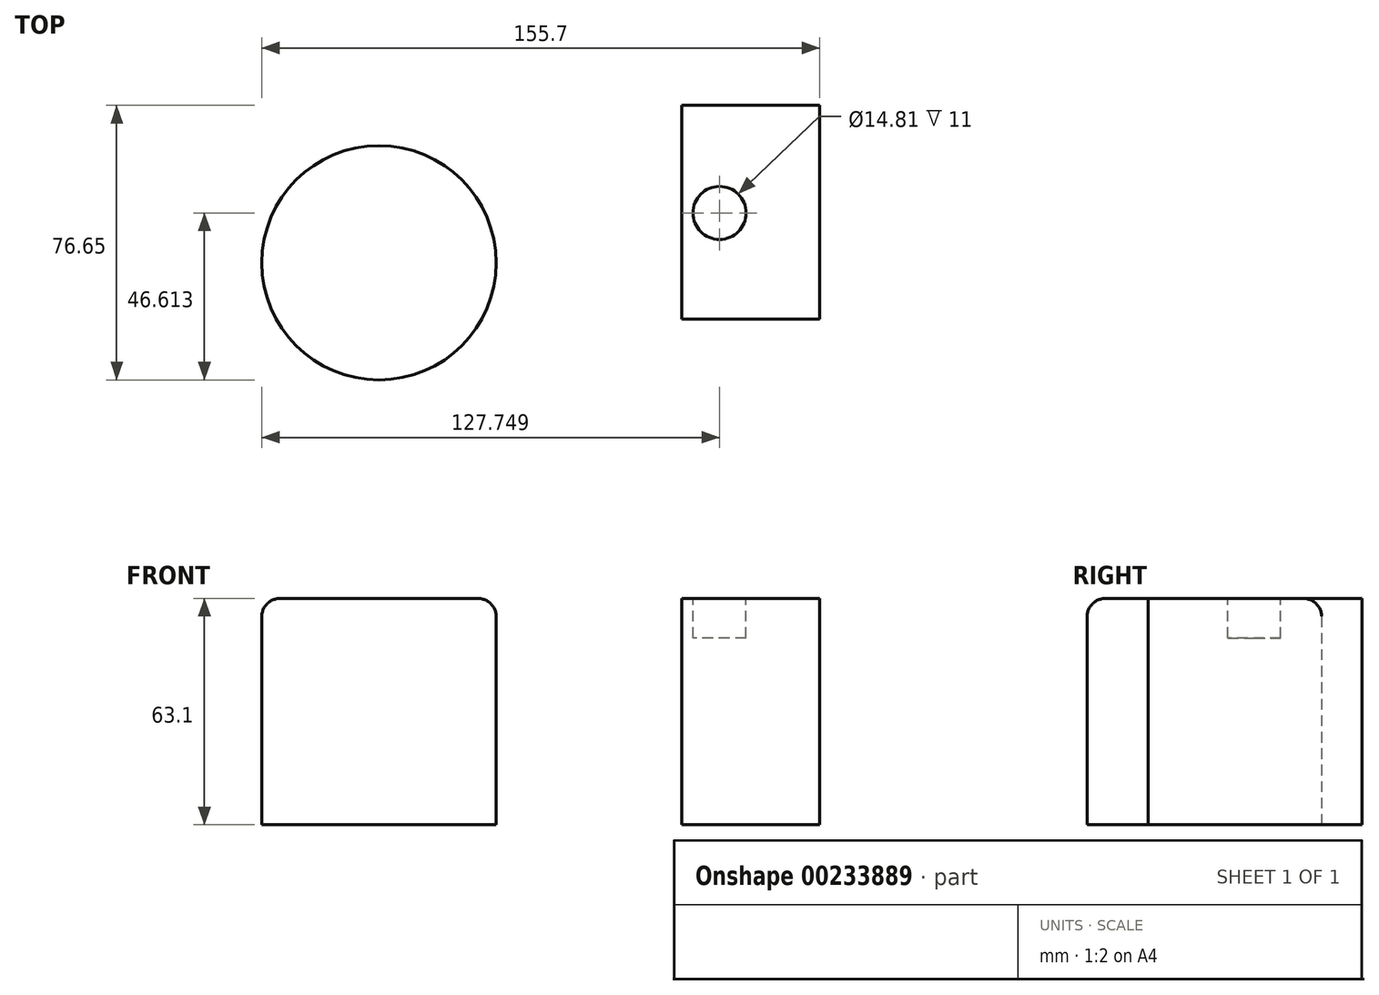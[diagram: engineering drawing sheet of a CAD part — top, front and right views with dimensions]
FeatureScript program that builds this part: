
annotation { "Feature Type Name" : "Feature", "Feature Type Description" : "" }
export const myFeature = defineFeature(function(context is Context, id is Id, definition is map)
    precondition{}
    {
        {
            var Q0;
            Q0=qCreatedBy(makeId("Top.planeOp"),FACE);
            var sketch = newSketch(context, id + "F0", { "sketchPlane" : qUnion([Q0])});
            skCircle(sketch, "E0", {"center": v(0, 0) * mm, "radius": 32.7 * mm});
            skLineSegment(sketch, "E1.bottom", {"start": v(84.57, -15.67) * mm, "end": v(123, -15.67) * mm});
            skLineSegment(sketch, "E1.top", {"start": v(84.57, 43.95) * mm, "end": v(123, 43.95) * mm});
            skLineSegment(sketch, "E1.left", {"start": v(84.57, -15.67) * mm, "end": v(84.57, 43.95) * mm});
            skLineSegment(sketch, "E1.right", {"start": v(123, -15.67) * mm, "end": v(123, 43.95) * mm});
            skLineSegment(sketch, "E2", {"start": v(148.77, 45.55) * mm, "end": v(148.77, 2.57) * mm});
            skLineSegment(sketch, "E3", {"start": v(0, 64.36) * mm, "end": v(5.98, 9.1) * mm});
            skLineSegment(sketch, "E4", {"start": v(73.85, 90.5) * mm, "end": v(77.86, 53.47) * mm});
            skLineSegment(sketch, "E5", {"start": v(-39.75, 64.85) * mm, "end": v(-32, -6.75) * mm});
            skSolve(sketch);
        }
        {
            var Q0;
            Q0=makeQuery(id+"F0.imprint","IMPRINT",FACE,{"disambiguationData":[TD([[makeQuery(id+"F0.imprint","IMPRINT",EDGE,{"derivedFrom":sQuery(id+"F0.wireOp",EDGE,"E0")}),1.0]])]});
            var Q1;
            Q1=makeQuery(id+"F0.imprint","IMPRINT",FACE,{"disambiguationData":[TD([[makeQuery(id+"F0.imprint","IMPRINT",EDGE,{"derivedFrom":sQuery(id+"F0.wireOp",EDGE,"E1.bottom")}),1.0]])]});
            extrude(context, id + "F1", {"entities" : qUnion([Q0, Q1]), "depth" : 63.1 * mm});
        }
        {
            var Q0;
            Q0=makeQuery(id+"F1.opExtrude","CAP_EDGE",EDGE,{"disambiguationData":[OSD([sQuery(id+"F0.wireOp",EDGE,"E0")])],"isStart":false});
            fillet(context, id + "F2", {"entities" : qUnion([Q0]), "radius" : 5 * mm, "tangentPropagation" : true, "allowEdgeOverflow" : false});
        }
        {
            var Q0;
            Q0=makeQuery(id+"F1.opExtrude","CAP_FACE",FACE,{"disambiguationData":[OSD([sQuery(id+"F0.wireOp",EDGE,"E1.bottom"),sQuery(id+"F0.wireOp",EDGE,"E1.top"),sQuery(id+"F0.wireOp",EDGE,"E1.left"),sQuery(id+"F0.wireOp",EDGE,"E1.right")])],"isStart":false});
            var sketch = newSketch(context, id + "F3", { "sketchPlane" : qUnion([Q0])});
            skCircle(sketch, "E6", {"center": v(95.05, 13.91) * mm, "radius": 7.4 * mm});
            skSolve(sketch);
        }
        {
            var Q0;
            Q0=makeQuery(id+"F3.imprint","IMPRINT",FACE,{"disambiguationData":[TD([[makeQuery(id+"F3.imprint","IMPRINT",EDGE,{"derivedFrom":sQuery(id+"F3.wireOp",EDGE,"E6")}),1.0]])]});
            extrude(context, id + "F4", {"entities" : qUnion([Q0]), "operationType" : NewBodyOperationType.REMOVE, "oppositeDirection" : true, "depth" : 11 * mm});
        }
    });
